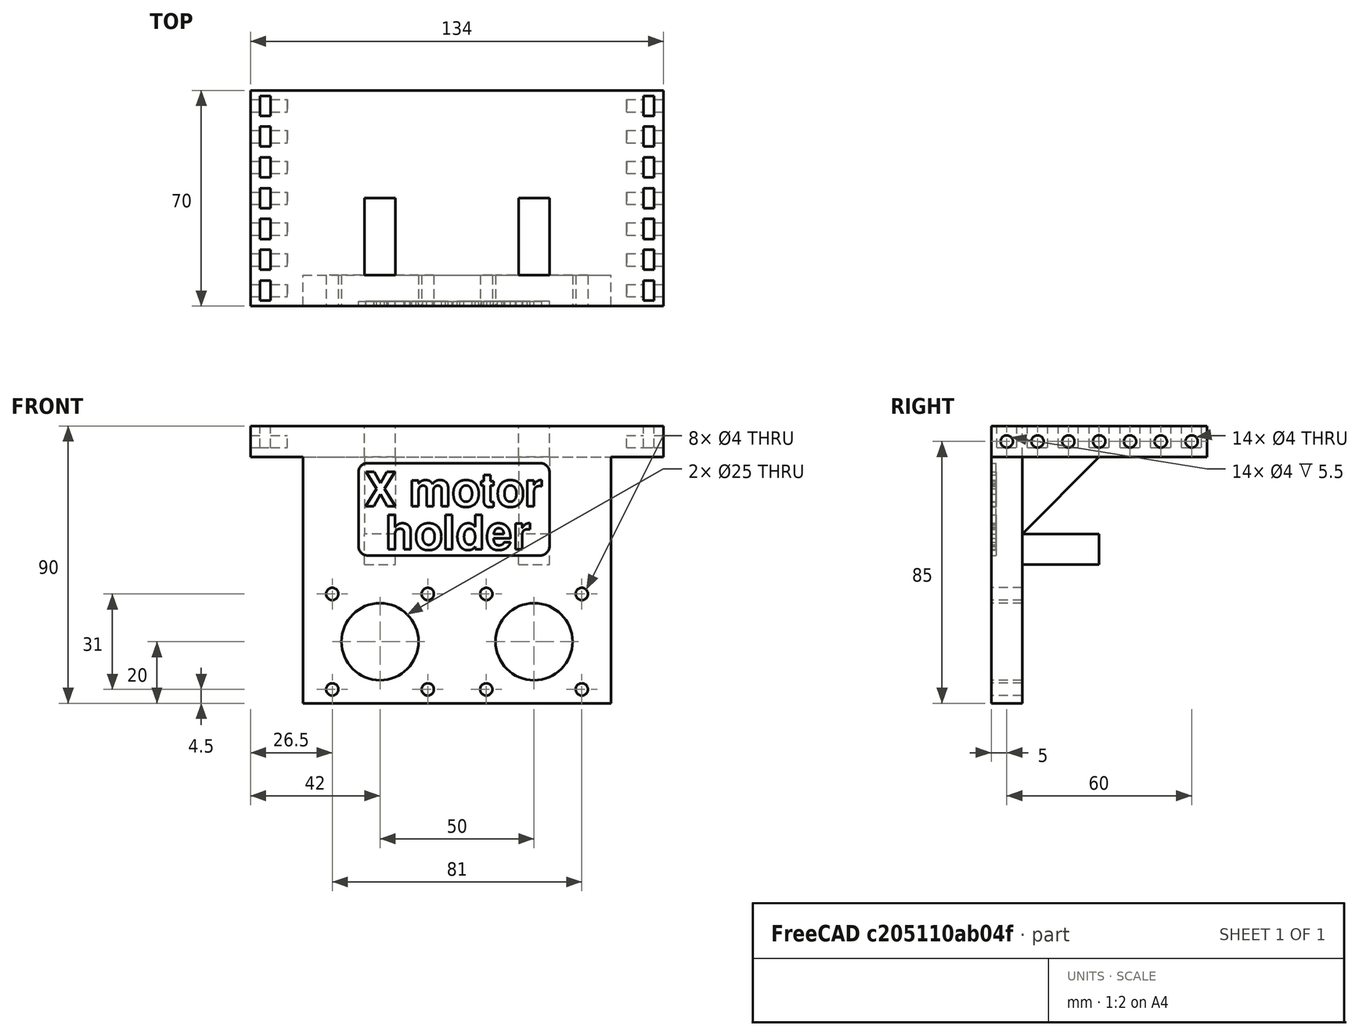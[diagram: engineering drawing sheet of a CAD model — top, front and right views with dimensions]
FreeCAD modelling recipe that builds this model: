
FCSTD DOCUMENT  (FreeCAD 0.14R3702 (Git))
Label: x_motor_holder
License: CC-BY 3.0
LicenseURL: http://creativecommons.org/licenses/by/3.0/
objects: Part::Feature×17, Part::Box×8, Part::Cylinder×5, Part::FeaturePython×4, Part::MultiFuse×4, Part::Part2DObjectPython×2, Part::Extrusion×2, Part::Fillet×1, Part::Cut×1
note: 44 computed .brp shape members not serialized (recipe doc carries the construction recipe); baked Part::Feature solids carry a one-line shape summary decoded from their .brp

FEATURE [Part::Box] Box  label="Cube"
  Height = 80
  Length = 100
  Width = 10
FEATURE [Part::Cylinder] Cylinder
  Angle = 360
  Height = 20
  Placement = pos=(25,17,20) rot=(1,0,0;1.5708rad)
  Radius = 12.5
FEATURE [Part::Cylinder] Cylinder001
  Angle = 360
  Height = 20
  Placement = pos=(75,17,20) rot=(1,0,0;1.5708rad)
  Radius = 12.5
FEATURE [Part::Cylinder] Cylinder002
  Angle = 360
  Height = 20
  Placement = pos=(9.5,17,4.5) rot=(1,0,0;1.5708rad)
  Radius = 2
FEATURE [Part::FeaturePython] Array  # Draft array (typed FeaturePython)
  Angle = 360
  ArrayType = 0
  Axis = (0,0,1)
  Base = -> Cylinder002
  Center = (0,0,0)
  IntervalX = (31,0,0)
  IntervalY = (0,3,0)
  IntervalZ = (0,0,31)
  NumberPolar = 1
  NumberX = 2
  NumberY = 1
  NumberZ = 2
FEATURE [Part::Cylinder] Cylinder003
  Angle = 360
  Height = 20
  Placement = pos=(9.5,17,4.5) rot=(1,0,0;1.5708rad)
  Radius = 2
FEATURE [Part::FeaturePython] Array001  # Draft array (typed FeaturePython)
  Angle = 360
  ArrayType = 0
  Axis = (0,0,1)
  Base = -> Cylinder003
  Center = (0,0,0)
  IntervalX = (31,0,0)
  IntervalY = (0,3,0)
  IntervalZ = (0,0,31)
  NumberPolar = 1
  NumberX = 2
  NumberY = 1
  NumberZ = 2
  Placement = pos=(50,0,0) rot=(0,0,1;0rad)
FEATURE [Part::Box] Box001  label="Cube001"
  Height = 10
  Length = 134
  Placement = pos=(-17,0,80) rot=(0,0,1;0rad)
  Width = 70
FEATURE [Part::Box] Box002  label="Cube002"
  Height = 10
  Length = 10
  Placement = pos=(20,10,80) rot=(0,0,1;0rad)
  Width = 25
FEATURE [Part::Box] Box003  label="Cube003"
  Height = 10
  Length = 10
  Placement = pos=(70,10,80) rot=(0,0,1;0rad)
  Width = 25
FEATURE [Part::Box] Box004  label="Cube004"
  Height = 10
  Length = 10
  Placement = pos=(70,10,45) rot=(0,0,1;0rad)
  Width = 25
FEATURE [Part::Box] Box005  label="Cube005"
  Height = 10
  Length = 10
  Placement = pos=(20,10,45) rot=(0,0,1;0rad)
  Width = 25
FEATURE [Part::Feature] Edge
  shape: bbox 2e-07 x 25 x 25 mm, 0 faces, 0 solids (baked)
FEATURE [Part::Feature] Edge001
  shape: bbox 2e-07 x 25 x 25 mm, 0 faces, 0 solids (baked)
FEATURE [Part::Feature] Edge002
  shape: bbox 10 x 2e-07 x 2e-07 mm, 0 faces, 0 solids (baked)
FEATURE [Part::Feature] Edge003
  shape: bbox 10 x 2e-07 x 2e-07 mm, 0 faces, 0 solids (baked)
FEATURE [Part::Feature] Edge004
  shape: bbox 2e-07 x 2e-07 x 25 mm, 0 faces, 0 solids (baked)
FEATURE [Part::Feature] Edge005
  shape: bbox 2e-07 x 2e-07 x 25 mm, 0 faces, 0 solids (baked)
FEATURE [Part::Feature] Edge006
  shape: bbox 10 x 2e-07 x 2e-07 mm, 0 faces, 0 solids (baked)
FEATURE [Part::Feature] Edge007
  shape: bbox 2e-07 x 25 x 2e-07 mm, 0 faces, 0 solids (baked)
FEATURE [Part::Feature] Edge008
  shape: bbox 2e-07 x 25 x 2e-07 mm, 0 faces, 0 solids (baked)
FEATURE [Part::Feature] Face
  shape: bbox 2e-07 x 41.25 x 41.25 mm, 1 faces, 0 solids (baked)
FEATURE [Part::Feature] Face001
  shape: bbox 2e-07 x 41.25 x 41.25 mm, 1 faces, 0 solids (baked)
FEATURE [Part::Feature] Face002
  shape: bbox 11 x 27.5 x 2e-07 mm, 1 faces, 0 solids (baked)
FEATURE [Part::Feature] Face003
  shape: bbox 11 x 2e-07 x 27.5 mm, 1 faces, 0 solids (baked)
FEATURE [Part::Feature] Face004
  shape: bbox 11 x 27.5 x 27.5 mm, 1 faces, 0 solids (baked)
FEATURE [Part::Feature] Shell
  shape: bbox 11 x 41.25 x 41.25 mm, 5 faces, 0 solids (baked)
FEATURE [Part::Feature] Shell_solid  label="s_nervio"
  shape: bbox 11 x 41.25 x 41.25 mm, 5 faces (baked)
FEATURE [Part::Feature] Shell_solid001  label="s_nervio001"
  Placement = pos=(-50,0,0) rot=(0,0,1;0rad)
  shape: bbox 11 x 41.25 x 41.25 mm, 5 faces (baked)
FEATURE [Part::Box] Box006  label="h_nut"
  Height = 8
  Length = 3.5
  Placement = pos=(-14,1.75,83) rot=(0,0,1;0rad)
  Width = 6.5
FEATURE [Part::Cylinder] Cylinder004
  Angle = 360
  Height = 13
  Placement = pos=(-18,5,85) rot=(0,1,0;1.5708rad)
  Radius = 2
FEATURE [Part::FeaturePython] Array002  label="h_nut001"  # Draft array (typed FeaturePython)
  Angle = 360
  ArrayType = 0
  Axis = (0,0,1)
  Base = -> Box006
  Center = (0,0,0)
  IntervalX = (124.5,0,0)
  IntervalY = (0,10,0)
  IntervalZ = (0,0,1)
  NumberPolar = 1
  NumberX = 2
  NumberY = 7
  NumberZ = 1
FEATURE [Part::FeaturePython] Array003  label="h_bolt"  # Draft array (typed FeaturePython)
  Angle = 360
  ArrayType = 0
  Axis = (0,0,1)
  Base = -> Cylinder004
  Center = (0,0,0)
  IntervalX = (123,0,0)
  IntervalY = (0,10,0)
  IntervalZ = (0,0,1)
  NumberPolar = 1
  NumberX = 2
  NumberY = 7
  NumberZ = 1
FEATURE [Part::MultiFuse] Fusion001  label="solid"
  Shapes = -> [Box,Box001,Shell_solid001,Shell_solid]
FEATURE [Part::Part2DObjectPython] ShapeString001  # Draft 2D object (typed FeaturePython)
  FontFile = <path>
  Placement = pos=(26.7571,0,50) rot=(1,0,0;1.5708rad)
  Size = 6
  String = holder
  Tracking = 0
FEATURE [Part::Part2DObjectPython] ShapeString  # Draft 2D object (typed FeaturePython)
  FontFile = <path>
  Placement = pos=(20,0,64) rot=(1,0,0;1.5708rad)
  Size = 6
  String = X motor
  Tracking = 0
FEATURE [Part::Extrusion] Extrude
  Base = -> ShapeString
  Dir = (0,1.5,0)
  Solid = true
FEATURE [Part::Extrusion] Extrude001
  Base = -> ShapeString001
  Dir = (0,1.5,0)
  Solid = true
FEATURE [Part::MultiFuse] Fusion002  label="s_txt"
  Shapes = -> [Extrude,Extrude001]
FEATURE [Part::Box] Box007  label="h_txt_groove"
  Height = 30
  Length = 62
  Placement = pos=(18,-1,48) rot=(0,0,1;0rad)
  Width = 2.5
FEATURE [Part::Fillet] Fillet  label="h_groove"
  Base = -> Box007
  Edges = 4 edges r=3: [Edge2,Edge4,Edge6,Edge8]
FEATURE [Part::MultiFuse] Fusion  label="hole"
  Shapes = -> [Fillet,Array002,Array003,Array001,Array,Cylinder001,Cylinder]
FEATURE [Part::Cut] Cut
  Base = -> Fusion001
  Tool = -> Fusion
FEATURE [Part::MultiFuse] Fusion003  label="x_motor_holder"
  Shapes = -> [Fusion002,Cut]
note: 2 file-system paths scrubbed to <path> (originals preserved in the JSON sidecar)
